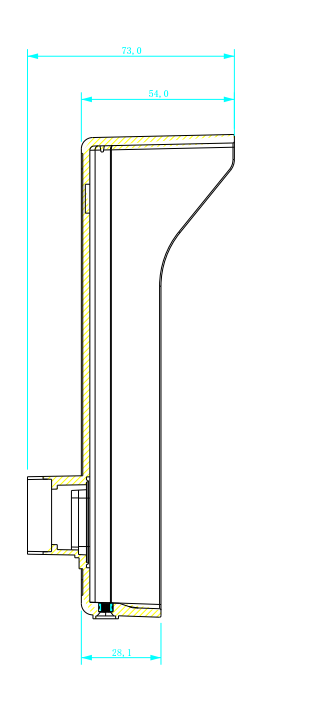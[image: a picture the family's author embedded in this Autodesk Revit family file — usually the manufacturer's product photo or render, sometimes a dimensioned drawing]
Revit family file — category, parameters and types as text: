
# Revit family: AT-10
name_source: partatom
category: Устройства связи
units: mm (PartAtom-declared; Revit-internal decimal feet)

## family parameters
Всегда вертикально = Нет
На основе рабочей плоскости = Да
Общий = Да
При загрузке вырезать с полостями = Нет
Размер круглого соединителя = Использовать диаметр
Сохранять ориентацию аннотаций = Нет
Тип детали = Нормальный
Точка принадлежности помещению = Нет

## types (1)
- AT-10
    ADSK_URL документации изделия = http://cdn.bas-ip.com
    ADSK_URL страницы изделия = https://www.bas-ip.ru
    ADSK_Версия Revit = Revit 2020
    ADSK_Единица измерения = шт
    ADSK_Завод-изготовитель = BAS-IP
    ADSK_Классификация нагрузок = Внутренний монитор индивидуальный
    ADSK_Количество фаз = 1
    ADSK_Коэффициент мощности = 0.9
    ADSK_Марка = AT-10
    ADSK_Наименование = Внутренний монитор индивидуальный AT-10
    ADSK_Наименование краткое = AT-10
    ADSK_Напряжение = 12 В
    ADSK_Номинальная мощность = 6 Вт
    ADSK_Полная мощность = 6 В·А
    ADSK_Размер_Длина = 185 мм
    ADSK_Размер_Толщина = 30 мм
    ADSK_Размер_Ширина = 316 мм
    BIM library = https://bimlib.ru
    URL = https://www.bas-ip.ru
    Автоответчик = Есть
    Бекап фото сделанных во время вызова = Есть, на SD карту
    Возможность установки сторонних приложений = Есть
    Встроенная камера = Есть
    Выбор типа заставки в режиме ожидания = Квадратор 
Часы 
Фоторамка 
Тур по времени 
IP камера (постоянный просмотр)
    Группа модели = Внутренний монитор индивидуальный AT-10
    Дисплей = 10” TFT LCD, сенсорный емкостный
    Дополнительные разъемы = Слот для microSD карт (SDHC)
    Загрузка пользовательских MP3 мелодий = Есть
    Изготовитель = BAS-IP
    Изображение типоразмера = <Нет>
    Интерфейс = Многоязычный графический и WEB-интерфейс
    Количество IP камер = До 32 камер
    Количество индивидуальных вызывных панелей = До 9 панелей
    Количество мелодий вызова = 9 мелодий на выбор
    Количество многоабонентских вызывных панелей = До 9 панелей
    Корпус = Алюминий, пластик
    Материал корпуса = Материал серый
    Мультимедиа возможности = Просмотр видео-, фото- и аудиофайлов с SD карты
    Обновление программного обеспечения = Через WEB-интерфейс, из SD карты, из сервера обновлений BAS-IP
    Описание = Внутренний монитор индивидуальный AT-10 - внутренний 10" IP-видеодомофон с IPS-экраном и разрешением 1280x800 и возможностью подключения датчиков тревоги. Внутренний видеодомофон работает на операционной системе Android 6.0. Он поставляется в 3 цветовых вариациях: белый, золотой, черный и имеет два варианты установки: настенное и скрытое крепление с помощью специального кронштейна.
    Отметка по умолчанию = 0 мм
    Питание = PoE  и +12 Вольт
    Поддержка получения сообщений = Есть
    Поддержка сторонних виджетов = Есть
    Подключение дополнительных мониторов = До 8 мониторов
    Потребление питания = 6 Вт, в режиме ожидания – 2,5 Вт
    Размеры = 316 x 185 x 29.5 мм
    Размеры дисплея = 218×137 мм
    Разрешение экрана = 1280 x 800
    Режим "Без звука" = Есть, настраиваемый по времени
    Режим "Не беспокоить" = Есть, настраиваемый по времени
    Режим "Ожидания" = Есть, настраиваемый по времени
    Сценарии = Есть
    Тип интеркома = Аудиоинтерком
    Тип установки = Настенная накладная, врезная с помощью кронштейна (опционально).
    Управление домашней автоматикой = Свет, шторы, лифт
    Функция памяти = Запись фото, видео и аудио на SD карту
    Цветовое решение = Black, White, Gold
